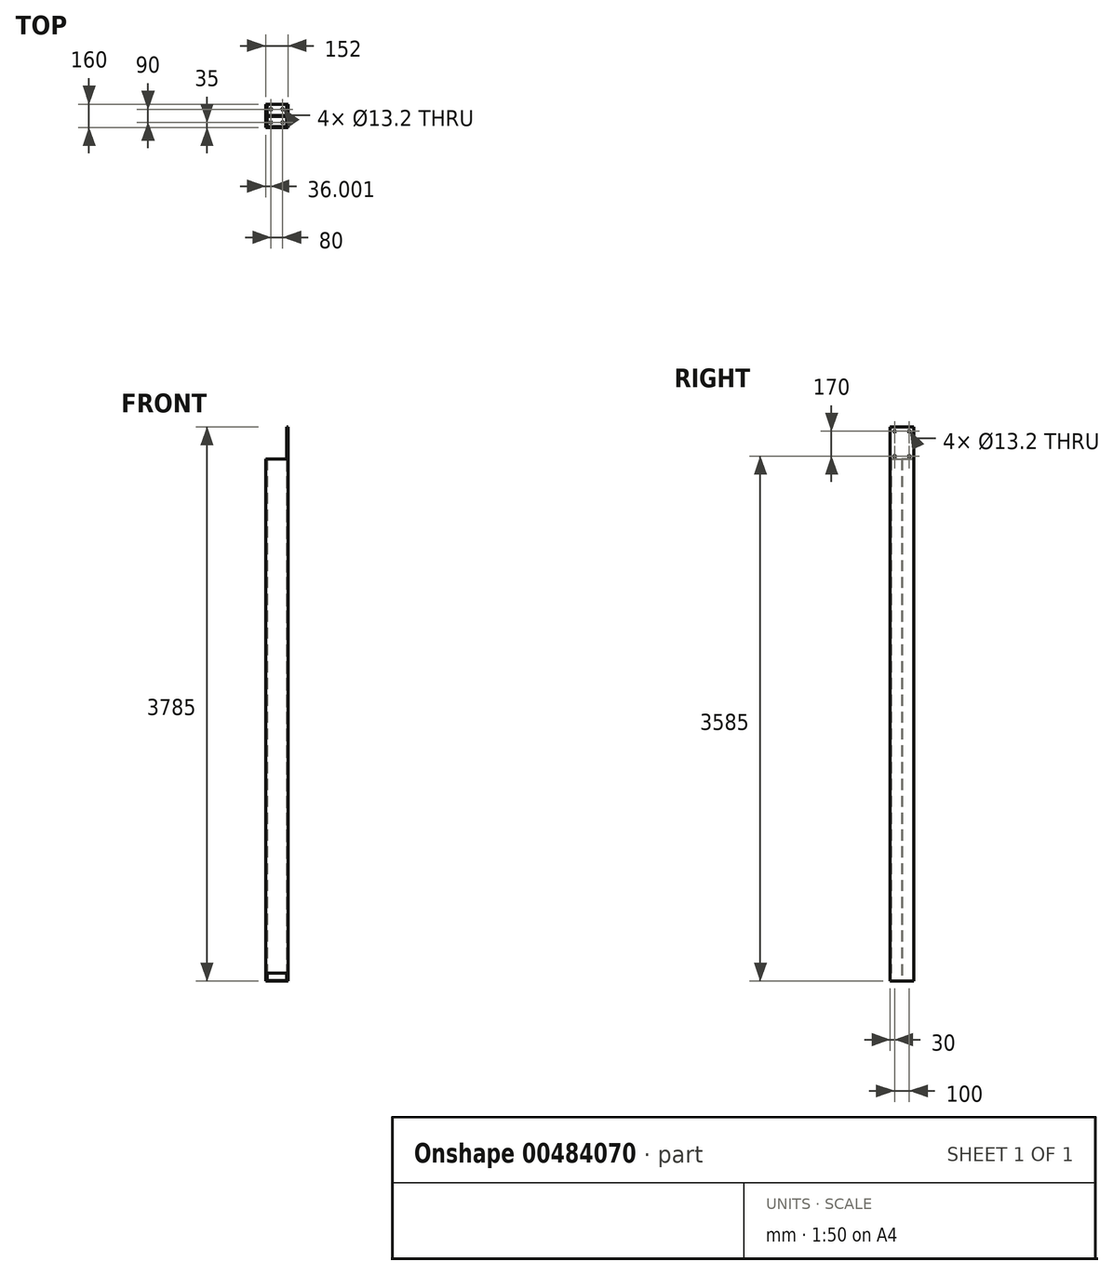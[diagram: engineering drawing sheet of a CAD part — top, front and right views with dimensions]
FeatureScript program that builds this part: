
annotation { "Feature Type Name" : "Feature", "Feature Type Description" : "" }
export const myFeature = defineFeature(function(context is Context, id is Id, definition is map)
    precondition{}
    {
        {
            var Q0;
            Q0=qCreatedBy(makeId("Top.planeOp"),FACE);
            var sketch = newSketch(context, id + "F0", { "sketchPlane" : qUnion([Q0])});
            skLineSegment(sketch, "E0", {"start": v(-170.58, -77) * mm, "end": v(-170.58, 83) * mm});
            skLineSegment(sketch, "E1", {"start": v(-170.58, 83) * mm, "end": v(-161.58, 83) * mm});
            skLineSegment(sketch, "E2", {"start": v(-161.58, 83) * mm, "end": v(-161.58, 6) * mm});
            skLineSegment(sketch, "E3", {"start": v(-161.58, 6) * mm, "end": v(-27.58, 6) * mm});
            skLineSegment(sketch, "E4", {"start": v(-27.58, 6) * mm, "end": v(-27.58, 83) * mm});
            skLineSegment(sketch, "E5", {"start": v(-27.58, 83) * mm, "end": v(-18.58, 83) * mm});
            skLineSegment(sketch, "E6", {"start": v(-18.58, 83) * mm, "end": v(-18.58, -77) * mm});
            skLineSegment(sketch, "E7", {"start": v(-18.58, -77) * mm, "end": v(-27.58, -77) * mm});
            skLineSegment(sketch, "E8", {"start": v(-27.58, -77) * mm, "end": v(-27.58, 0) * mm});
            skLineSegment(sketch, "E9", {"start": v(-27.58, 0) * mm, "end": v(-161.58, 0) * mm});
            skLineSegment(sketch, "E10", {"start": v(-161.58, 0) * mm, "end": v(-161.58, -77) * mm});
            skLineSegment(sketch, "E11", {"start": v(-161.58, -77) * mm, "end": v(-170.58, -77) * mm});
            skSolve(sketch);
        }
        {
            var Q0;
            Q0 = qSketchRegion(id + "F0", true);
            extrude(context, id + "F1", {"entities" : qUnion([Q0]), "depth" : 3785 * mm, "offsetDistance" : 25 * mm});
        }
        {
            var Q0;
            Q0=makeQuery(id+"F1.opExtrude","SWEPT_FACE",FACE,{"disambiguationData":[OSD([sQuery(id+"F0.wireOp",EDGE,"E9")])]});
            var sketch = newSketch(context, id + "F2", { "sketchPlane" : qUnion([Q0])});
            skLineSegment(sketch, "E12.bottom", {"start": v(-161.58, 3785) * mm, "end": v(-27.58, 3785) * mm});
            skLineSegment(sketch, "E12.top", {"start": v(-161.58, 3565) * mm, "end": v(-27.58, 3565) * mm});
            skLineSegment(sketch, "E12.left", {"start": v(-161.58, 3785) * mm, "end": v(-161.58, 3565) * mm});
            skLineSegment(sketch, "E12.right", {"start": v(-27.58, 3785) * mm, "end": v(-27.58, 3565) * mm});
            skSolve(sketch);
        }
        {
            var Q0;
            Q0 = qSketchRegion(id + "F2", true);
            extrude(context, id + "F3", {"entities" : qUnion([Q0]), "operationType" : NewBodyOperationType.REMOVE, "oppositeDirection" : true, "depth" : 100 * mm, "offsetDistance" : 25 * mm});
        }
        {
            var Q0;
            Q0=makeQuery(id+"F1.opExtrude","SWEPT_FACE",FACE,{"disambiguationData":[OSD([sQuery(id+"F0.wireOp",EDGE,"E0")])]});
            var sketch = newSketch(context, id + "F4", { "sketchPlane" : qUnion([Q0])});
            skLineSegment(sketch, "E13.bottom", {"start": v(-83, 3785) * mm, "end": v(77, 3785) * mm});
            skLineSegment(sketch, "E13.top", {"start": v(-83, 3565) * mm, "end": v(77, 3565) * mm});
            skLineSegment(sketch, "E13.left", {"start": v(-83, 3785) * mm, "end": v(-83, 3565) * mm});
            skLineSegment(sketch, "E13.right", {"start": v(77, 3785) * mm, "end": v(77, 3565) * mm});
            skSolve(sketch);
        }
        {
            var Q0;
            Q0 = qSketchRegion(id + "F4", true);
            extrude(context, id + "F5", {"entities" : qUnion([Q0]), "operationType" : NewBodyOperationType.REMOVE, "oppositeDirection" : true, "depth" : 25 * mm, "offsetDistance" : 25 * mm});
        }
        {
            var Q0;
            Q0=makeQuery(id+"F1.opExtrude","SWEPT_FACE",FACE,{"disambiguationData":[OSD([sQuery(id+"F0.wireOp",EDGE,"E6")])]});
            var sketch = newSketch(context, id + "F6", { "sketchPlane" : qUnion([Q0])});
            skLineSegment(sketch, "E14", {"start": v(-77, 3785) * mm, "end": v(-47, 3785) * mm});
            skLineSegment(sketch, "E15", {"start": v(-47, 3785) * mm, "end": v(-47, 3755) * mm});
            skLineSegment(sketch, "E16", {"start": v(-47, 3755) * mm, "end": v(53, 3755) * mm});
            skLineSegment(sketch, "E17", {"start": v(53, 3755) * mm, "end": v(53, 3585) * mm});
            skLineSegment(sketch, "E18", {"start": v(53, 3585) * mm, "end": v(-47, 3585) * mm});
            skSolve(sketch);
        }
        {
            var Q0;
            Q0=sQuery(id+"F6.wireOp",VERTEX,"E16.start");
            var Q1;
            Q1=sQuery(id+"F6.wireOp",VERTEX,"E17.start");
            var Q2;
            Q2=sQuery(id+"F6.wireOp",VERTEX,"E18.end");
            var Q3;
            Q3=sQuery(id+"F6.wireOp",VERTEX,"E17.end");
            var Q4;
            Q4=makeQuery(id+"F1.opExtrude","SWEPT_BODY",BODY,{"disambiguationData":[OSD([sQuery(id+"F0.wireOp",EDGE,"E0"),sQuery(id+"F0.wireOp",EDGE,"E1"),sQuery(id+"F0.wireOp",EDGE,"E2"),sQuery(id+"F0.wireOp",EDGE,"E3"),sQuery(id+"F0.wireOp",EDGE,"E4"),sQuery(id+"F0.wireOp",EDGE,"E5"),sQuery(id+"F0.wireOp",EDGE,"E6"),sQuery(id+"F0.wireOp",EDGE,"E7"),sQuery(id+"F0.wireOp",EDGE,"E8"),sQuery(id+"F0.wireOp",EDGE,"E9"),sQuery(id+"F0.wireOp",EDGE,"E10"),sQuery(id+"F0.wireOp",EDGE,"E11")])]});
            hole(context, id + "F7", {"style" : HoleStyle.SIMPLE, "endStyle" : HoleEndStyle.THROUGH, "standardTappedOrClearance" : lookupTablePath({ "standard" : "ISO", "fit" : "Normal", "size" : "M12", "type" : "Clearance" }), "standardBlindInLast" : lookupTablePath({ "fit" : "Standard", "standard" : "ISO", "size" : "M12", "type" : "Clearance" }), "holeDiameter" : 13.2 * mm, "isTappedThrough" : true, "tappedDepth" : 12 * mm, "tapClearance" : 3, "locations" : qUnion([Q0, Q1, Q2, Q3]), "scope" : qUnion([Q4])});
        }
        {
            var Q0;
            Q0=makeQuery(id+"F1.opExtrude","SWEPT_FACE",FACE,{"disambiguationData":[OSD([sQuery(id+"F0.wireOp",EDGE,"E3")])]});
            var sketch = newSketch(context, id + "F8", { "sketchPlane" : qUnion([Q0])});
            skLineSegment(sketch, "E19.bottom", {"start": v(27.58, 0) * mm, "end": v(161.58, 0) * mm});
            skLineSegment(sketch, "E19.top", {"start": v(27.58, 5) * mm, "end": v(161.58, 5) * mm});
            skLineSegment(sketch, "E19.left", {"start": v(27.58, 0) * mm, "end": v(27.58, 5) * mm});
            skLineSegment(sketch, "E19.right", {"start": v(161.58, 0) * mm, "end": v(161.58, 5) * mm});
            skSolve(sketch);
        }
        {
            var Q0;
            Q0 = qSketchRegion(id + "F8", true);
            extrude(context, id + "F9", {"entities" : qUnion([Q0]), "operationType" : NewBodyOperationType.ADD, "depth" : 77 * mm, "offsetDistance" : 25 * mm});
        }
        {
            var Q0;
            Q0=makeQuery(id+"F1.opExtrude","SWEPT_FACE",FACE,{"disambiguationData":[OSD([sQuery(id+"F0.wireOp",EDGE,"E9")])]});
            var sketch = newSketch(context, id + "F10", { "sketchPlane" : qUnion([Q0])});
            skLineSegment(sketch, "E20.bottom", {"start": v(-27.58, 0) * mm, "end": v(-161.58, 0) * mm});
            skLineSegment(sketch, "E20.top", {"start": v(-27.58, 5) * mm, "end": v(-161.58, 5) * mm});
            skLineSegment(sketch, "E20.left", {"start": v(-27.58, 0) * mm, "end": v(-27.58, 5) * mm});
            skLineSegment(sketch, "E20.right", {"start": v(-161.58, 0) * mm, "end": v(-161.58, 5) * mm});
            skSolve(sketch);
        }
        {
            var Q0;
            Q0 = qSketchRegion(id + "F10", true);
            extrude(context, id + "F11", {"entities" : qUnion([Q0]), "operationType" : NewBodyOperationType.ADD, "depth" : 77 * mm, "offsetDistance" : 25 * mm});
        }
        {
            var Q0;
            Q0=makeQuery(id+"F11.boolean.opBoolean","MERGE",FACE,{"derivedFrom":[makeQuery(id+"F9.boolean.opBoolean","MERGE",FACE,{"derivedFrom":[makeQuery(id+"F1.opExtrude","CAP_FACE",FACE,{"disambiguationData":[OSD([sQuery(id+"F0.wireOp",EDGE,"E0"),sQuery(id+"F0.wireOp",EDGE,"E1"),sQuery(id+"F0.wireOp",EDGE,"E2"),sQuery(id+"F0.wireOp",EDGE,"E3"),sQuery(id+"F0.wireOp",EDGE,"E4"),sQuery(id+"F0.wireOp",EDGE,"E5"),sQuery(id+"F0.wireOp",EDGE,"E6"),sQuery(id+"F0.wireOp",EDGE,"E7"),sQuery(id+"F0.wireOp",EDGE,"E8"),sQuery(id+"F0.wireOp",EDGE,"E9"),sQuery(id+"F0.wireOp",EDGE,"E10"),sQuery(id+"F0.wireOp",EDGE,"E11")])],"isStart":true}),makeQuery(id+"F9.opExtrude","SWEPT_FACE",FACE,{"disambiguationData":[OSD([sQuery(id+"F8.wireOp",EDGE,"E19.bottom")])]})]}),makeQuery(id+"F11.opExtrude","SWEPT_FACE",FACE,{"disambiguationData":[OSD([sQuery(id+"F10.wireOp",EDGE,"E20.bottom")])]})]});
            var sketch = newSketch(context, id + "F12", { "sketchPlane" : qUnion([Q0])});
            skLineSegment(sketch, "E21", {"start": v(-94.58, -83) * mm, "end": v(-94.58, -48) * mm});
            skLineSegment(sketch, "E22", {"start": v(-94.58, -48) * mm, "end": v(-54.58, -48) * mm});
            skLineSegment(sketch, "E23", {"start": v(-94.58, -48) * mm, "end": v(-134.58, -48) * mm});
            skLineSegment(sketch, "E24", {"start": v(-94.58, 77) * mm, "end": v(-94.58, 42) * mm});
            skLineSegment(sketch, "E25", {"start": v(-94.58, 42) * mm, "end": v(-54.58, 42) * mm});
            skLineSegment(sketch, "E26", {"start": v(-94.58, 42) * mm, "end": v(-134.58, 42) * mm});
            skSolve(sketch);
        }
        {
            var Q0;
            Q0=sQuery(id+"F12.wireOp",VERTEX,"E22.end");
            var Q1;
            Q1=sQuery(id+"F12.wireOp",VERTEX,"E25.end");
            var Q2;
            Q2=sQuery(id+"F12.wireOp",VERTEX,"E26.end");
            var Q3;
            Q3=sQuery(id+"F12.wireOp",VERTEX,"E23.end");
            var Q4;
            Q4=makeQuery(id+"F1.opExtrude","SWEPT_BODY",BODY,{"disambiguationData":[OSD([sQuery(id+"F0.wireOp",EDGE,"E0"),sQuery(id+"F0.wireOp",EDGE,"E1"),sQuery(id+"F0.wireOp",EDGE,"E2"),sQuery(id+"F0.wireOp",EDGE,"E3"),sQuery(id+"F0.wireOp",EDGE,"E4"),sQuery(id+"F0.wireOp",EDGE,"E5"),sQuery(id+"F0.wireOp",EDGE,"E6"),sQuery(id+"F0.wireOp",EDGE,"E7"),sQuery(id+"F0.wireOp",EDGE,"E8"),sQuery(id+"F0.wireOp",EDGE,"E9"),sQuery(id+"F0.wireOp",EDGE,"E10"),sQuery(id+"F0.wireOp",EDGE,"E11")])]});
            hole(context, id + "F13", {"style" : HoleStyle.SIMPLE, "endStyle" : HoleEndStyle.THROUGH, "standardTappedOrClearance" : lookupTablePath({ "standard" : "ISO", "fit" : "Normal", "size" : "M12", "type" : "Clearance" }), "standardBlindInLast" : lookupTablePath({ "fit" : "Standard", "standard" : "ISO", "size" : "M12", "type" : "Clearance" }), "holeDiameter" : 13.2 * mm, "isTappedThrough" : true, "tappedDepth" : 12 * mm, "tapClearance" : 3, "locations" : qUnion([Q0, Q1, Q2, Q3]), "scope" : qUnion([Q4])});
        }
        {
            var Q0;
            Q0=makeQuery(id+"F11.boolean.opBoolean","MERGE",FACE,{"derivedFrom":[makeQuery(id+"F1.opExtrude","SWEPT_FACE",FACE,{"disambiguationData":[OSD([sQuery(id+"F0.wireOp",EDGE,"E7")])]}),makeQuery(id+"F1.opExtrude","SWEPT_FACE",FACE,{"disambiguationData":[OSD([sQuery(id+"F0.wireOp",EDGE,"E11")])]}),makeQuery(id+"F11.opExtrude","CAP_FACE",FACE,{"disambiguationData":[OSD([sQuery(id+"F10.wireOp",EDGE,"E20.bottom"),sQuery(id+"F10.wireOp",EDGE,"E20.top"),sQuery(id+"F10.wireOp",EDGE,"E20.left"),sQuery(id+"F10.wireOp",EDGE,"E20.right")])],"isStart":false})]});
            var sketch = newSketch(context, id + "F14", { "sketchPlane" : qUnion([Q0])});
            skLineSegment(sketch, "E27.bottom", {"start": v(-161.58, 3565) * mm, "end": v(-27.58, 3565) * mm});
            skLineSegment(sketch, "E27.top", {"start": v(-161.58, 55) * mm, "end": v(-27.58, 55) * mm});
            skLineSegment(sketch, "E27.left", {"start": v(-161.58, 3565) * mm, "end": v(-161.58, 55) * mm});
            skLineSegment(sketch, "E27.right", {"start": v(-27.58, 3565) * mm, "end": v(-27.58, 55) * mm});
            skSolve(sketch);
        }
        {
            var Q0;
            Q0 = qSketchRegion(id + "F14", true);
            extrude(context, id + "F15", {"entities" : qUnion([Q0]), "operationType" : NewBodyOperationType.ADD, "depth" : -5 * mm, "offsetDistance" : 25 * mm});
        }
    });
